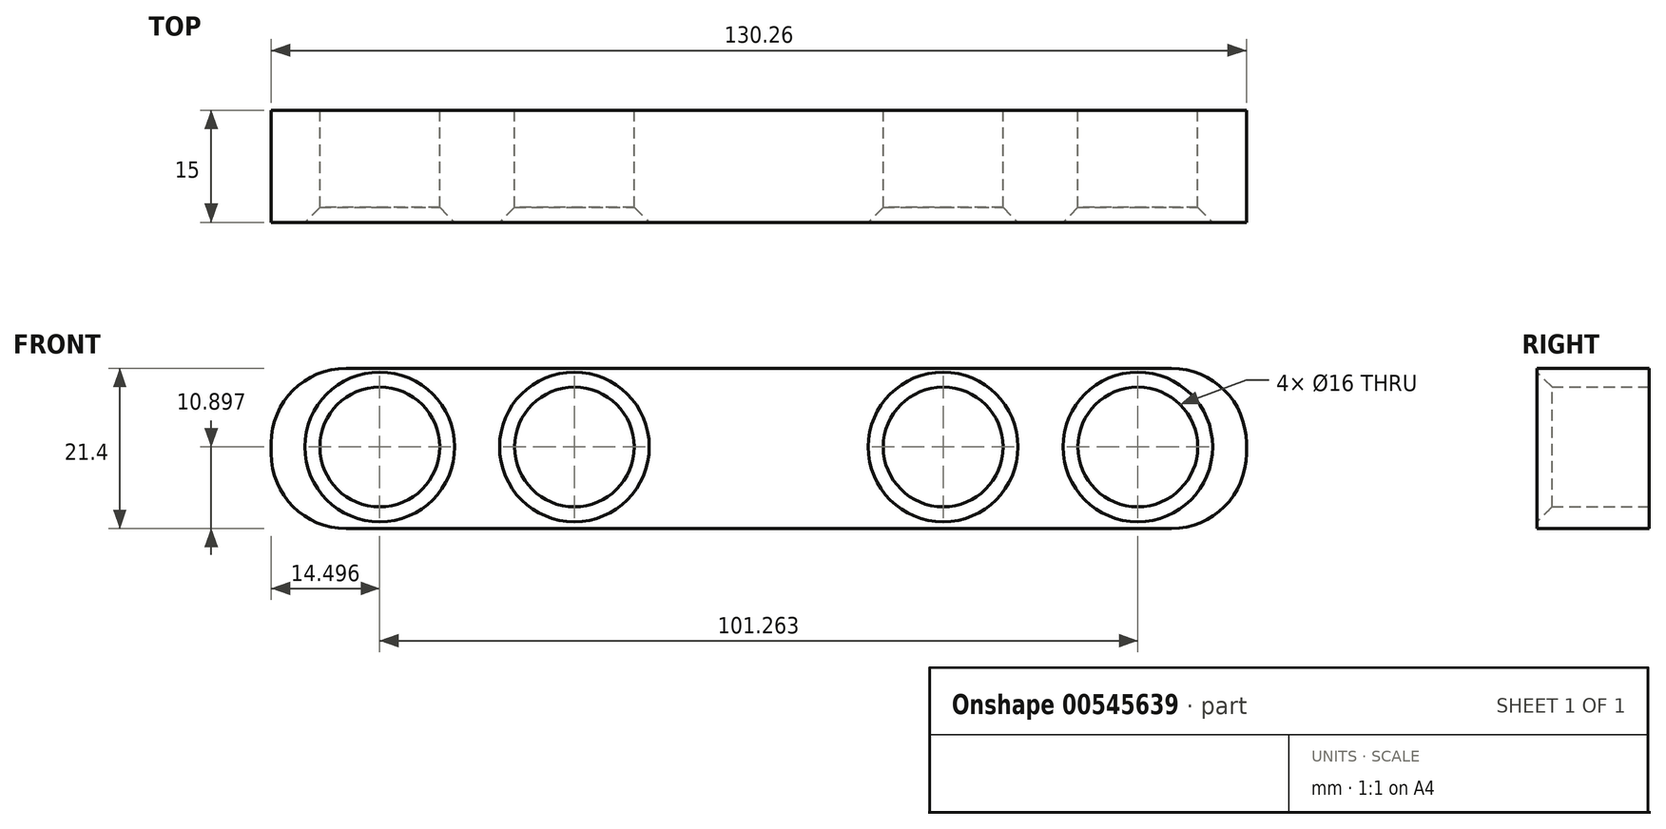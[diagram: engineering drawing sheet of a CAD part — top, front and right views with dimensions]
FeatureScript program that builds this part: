
annotation { "Feature Type Name" : "Feature", "Feature Type Description" : "" }
export const myFeature = defineFeature(function(context is Context, id is Id, definition is map)
    precondition{}
    {
        {
            var Q0;
            Q0=qCreatedBy(makeId("Front.planeOp"),FACE);
            var sketch = newSketch(context, id + "F0", { "sketchPlane" : qUnion([Q0])});
            skLineSegment(sketch, "E0.bottom", {"start": v(-66.46, 38.42) * mm, "end": v(63.8, 38.42) * mm});
            skLineSegment(sketch, "E0.top", {"start": v(-66.46, 17.02) * mm, "end": v(63.8, 17.02) * mm});
            skLineSegment(sketch, "E0.left", {"start": v(-66.46, 38.42) * mm, "end": v(-66.46, 17.02) * mm});
            skLineSegment(sketch, "E0.right", {"start": v(63.8, 38.42) * mm, "end": v(63.8, 17.02) * mm});
            skCircle(sketch, "E1", {"center": v(-51.96, 27.92) * mm, "radius": 8 * mm});
            skCircle(sketch, "E2", {"center": v(-25.96, 27.92) * mm, "radius": 8 * mm});
            skCircle(sketch, "E3", {"center": v(23.3, 27.92) * mm, "radius": 8 * mm});
            skCircle(sketch, "E4", {"center": v(49.3, 27.92) * mm, "radius": 8 * mm});
            skSolve(sketch);
        }
        {
            var Q0;
            Q0=makeQuery(id+"F0.imprint","IMPRINT",FACE,{"disambiguationData":[TD([[makeQuery(id+"F0.imprint","IMPRINT",EDGE,{"derivedFrom":sQuery(id+"F0.wireOp",EDGE,"E0.bottom")}),-1.0]])]});
            extrude(context, id + "F1", {"entities" : qUnion([Q0]), "depth" : 15 * mm, "offsetDistance" : 25 * mm});
        }
        {
            var Q0;
            Q0=makeQuery(id+"F1.opExtrude","SWEPT_EDGE",EDGE,{"disambiguationData":[OSD([sQuery(id+"F0.wireOp",EDGE,"E0.bottom"),sQuery(id+"F0.wireOp",EDGE,"E0.right")])]});
            var Q1;
            Q1=makeQuery(id+"F1.opExtrude","SWEPT_EDGE",EDGE,{"disambiguationData":[OSD([sQuery(id+"F0.wireOp",EDGE,"E0.top"),sQuery(id+"F0.wireOp",EDGE,"E0.right")])]});
            var Q2;
            Q2=makeQuery(id+"F1.opExtrude","SWEPT_EDGE",EDGE,{"disambiguationData":[OSD([sQuery(id+"F0.wireOp",EDGE,"E0.bottom"),sQuery(id+"F0.wireOp",EDGE,"E0.left")])]});
            var Q3;
            Q3=makeQuery(id+"F1.opExtrude","SWEPT_EDGE",EDGE,{"disambiguationData":[OSD([sQuery(id+"F0.wireOp",EDGE,"E0.top"),sQuery(id+"F0.wireOp",EDGE,"E0.left")])]});
            fillet(context, id + "F2", {"entities" : qUnion([Q0, Q1, Q2, Q3]), "radius" : 10 * mm, "tangentPropagation" : true, "allowEdgeOverflow" : false});
        }
        {
            var Q0;
            Q0=makeQuery(id+"F1.opExtrude","CAP_EDGE",EDGE,{"disambiguationData":[OSD([sQuery(id+"F0.wireOp",EDGE,"E2")])],"isStart":false});
            var Q1;
            Q1=makeQuery(id+"F1.opExtrude","CAP_EDGE",EDGE,{"disambiguationData":[OSD([sQuery(id+"F0.wireOp",EDGE,"E3")])],"isStart":false});
            var Q2;
            Q2=makeQuery(id+"F1.opExtrude","CAP_EDGE",EDGE,{"disambiguationData":[OSD([sQuery(id+"F0.wireOp",EDGE,"E4")])],"isStart":false});
            var Q3;
            Q3=makeQuery(id+"F1.opExtrude","CAP_EDGE",EDGE,{"disambiguationData":[OSD([sQuery(id+"F0.wireOp",EDGE,"E1")])],"isStart":false});
            chamfer(context, id + "F3", {"entities" : qUnion([Q0, Q1, Q2, Q3]), "width" : 2 * mm, "tangentPropagation" : true});
        }
    });
